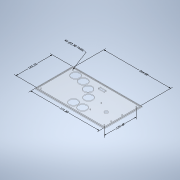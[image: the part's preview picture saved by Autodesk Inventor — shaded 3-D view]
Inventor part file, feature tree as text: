
AUTODESK INVENTOR PART (.ipt)
format: ipt  version: 2022 (Build 260153000, 153)  size: 240,128 bytes
history: native  units: mm
features: extrude x7, sketch x7, other x5, mirror x2, hole x1
ambient origin geometry x8: Origin, YZ Plane, XZ Plane, XY Plane, X Axis, Y Axis, Z Axis, Center Point
bodies: Solid1 (feature_tree)
feature tree (22):
  other  "Annotations"
  extrude  "Bottom_Base"  Depth=3.572mm
  extrude  "Side_Insert"  Depth=1.5875mm
  mirror  "Mirrored_Side_Insert"
  extrude  "Front_Insert"  Depth=3.572mm
  mirror  "Back_Insert"
  extrude  "Joint_Holes"  Depth=0.8mm TaperAngle=0.0deg
  extrude  "Joystick_Mounting_Holes"  Depth=6.6mm
  extrude  "Button_Mounting_Holes"  Depth=6.6mm
  extrude  "USB_Access"  TaperAngle=0.0deg  [1 undecoded]
  sketch  "Sketch1"  dims[d2=0.0mm d3=3.572mm]
  sketch  "Sketch2"  dims[d4=1.5875mm d5=1.5875mm]
  sketch  "Sketch3"  dims[d6=0.8mm d7=0.0mm d8=3.572mm]
  sketch  "Sketch4"  dims[d9=1.5875mm d10=0.8mm d11=0.0mm]
  sketch  "Sketch5"  dims[d18=3.3mm d19=6.6mm]
  sketch  "Sketch6"  dims[d20=6.6mm d21=6.6mm]
  sketch  "Sketch7"  dims[d22=6.6mm d23=0.0mm d24=0.0mm d27=275.0mm d32=126.481mm d34=82.08mm d35=43.55mm d36=3.3mm d37=12.5mm d38=84.7005mm d39=15.0mm d40=10.0mm d41=0.0mm d42=124.0mm d43=96.0mm d44=128.083333mm d45=42.0mm d46=33.0mm d47=36.0mm d48=30.0mm d49=46.0mm d50=36.0mm d51=0.0mm d52=0.0mm d53=24.0mm d54=8.0mm d55=16.0mm d56=0.0mm d57=0.0mm d12=0.167694mm d13=0.260382mm d14=143.253mm d15=8.279997mm d16=0.523652mm d17=264.681mm d25=55.304283mm d28=8.303899mm d29=0.853148mm d30=271.825mm d33=126.481mm]
  other  "Linear Dimension 1"
  other  "Linear Dimension 2"
  hole  "Hole Note 1"  [1 undecoded]
  other  "Linear Dimension 3"
  other  "Linear Dimension 4"
note: 2 required parameter values undecoded (feature->parameter linkage not recoverable at this tier; creation-order binding heuristic only, values carry confidence <= 0.55)
